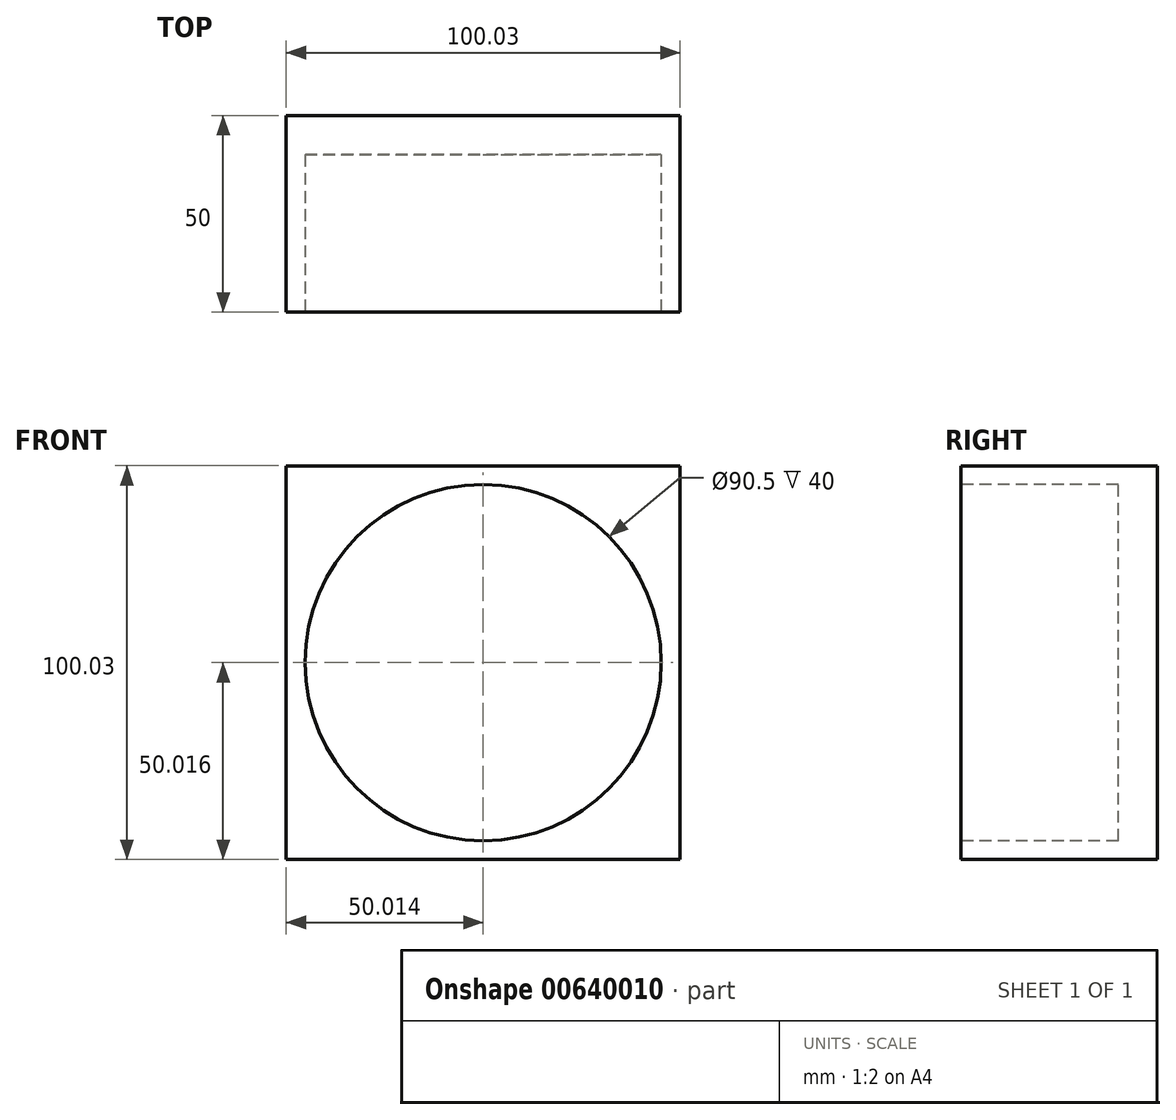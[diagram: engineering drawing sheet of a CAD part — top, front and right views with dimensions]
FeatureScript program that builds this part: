
annotation { "Feature Type Name" : "Feature", "Feature Type Description" : "" }
export const myFeature = defineFeature(function(context is Context, id is Id, definition is map)
    precondition{}
    {
        {
            var Q0;
            Q0=qCreatedBy(makeId("Front.planeOp"),FACE);
            var sketch = newSketch(context, id + "F0", { "sketchPlane" : qUnion([Q0])});
            skLineSegment(sketch, "E0.bottom", {"start": v(-42.27, 42.27) * mm, "end": v(57.76, 42.27) * mm});
            skLineSegment(sketch, "E0.top", {"start": v(-42.27, -57.76) * mm, "end": v(57.76, -57.76) * mm});
            skLineSegment(sketch, "E0.left", {"start": v(-42.27, 42.27) * mm, "end": v(-42.27, -57.76) * mm});
            skLineSegment(sketch, "E0.right", {"start": v(57.76, 42.27) * mm, "end": v(57.76, -57.76) * mm});
            skSolve(sketch);
        }
        {
            var Q0;
            Q0=makeQuery(id+"F0.imprint","IMPRINT",FACE,{"disambiguationData":[TD([[makeQuery(id+"F0.imprint","IMPRINT",EDGE,{"derivedFrom":sQuery(id+"F0.wireOp",EDGE,"E0.bottom")}),-1.0]])]});
            extrude(context, id + "F1", {"entities" : qUnion([Q0]), "depth" : 50 * mm, "offsetDistance" : 25 * mm});
        }
        {
            var Q0;
            Q0=makeQuery(id+"F1.opExtrude","CAP_FACE",FACE,{"disambiguationData":[OSD([sQuery(id+"F0.wireOp",EDGE,"E0.bottom"),sQuery(id+"F0.wireOp",EDGE,"E0.top"),sQuery(id+"F0.wireOp",EDGE,"E0.left"),sQuery(id+"F0.wireOp",EDGE,"E0.right")])],"isStart":false});
            var sketch = newSketch(context, id + "F2", { "sketchPlane" : qUnion([Q0])});
            skCircle(sketch, "E1", {"center": v(7.74, -7.74) * mm, "radius": 45.25 * mm});
            skPoint(sketch, "E1.centerSnap0", {"position": v(57.76, -7.74) * mm});
            skPoint(sketch, "E1.centerSnap1", {"position": v(7.74, -57.76) * mm});
            skSolve(sketch);
        }
        {
            var Q0;
            Q0=makeQuery(id+"F2.imprint","IMPRINT",FACE,{"disambiguationData":[TD([[makeQuery(id+"F2.imprint","IMPRINT",EDGE,{"derivedFrom":sQuery(id+"F2.wireOp",EDGE,"E1")}),1.0]])]});
            extrude(context, id + "F3", {"entities" : qUnion([Q0]), "operationType" : NewBodyOperationType.REMOVE, "oppositeDirection" : true, "depth" : 40 * mm, "offsetDistance" : 25 * mm});
        }
    });
